# Revit family: Gira_004200
name_source: partatom
category: Electrical Fixtures
revit_build: Autodesk Revit 2017 (Build: 20160225_1515(x64)
units: mm (PartAtom-declared; Revit-internal decimal feet)

## family parameters
Cut with Voids When Loaded = No
Host = Face
Maintain Annotation Orientation = Yes
Part Type = Normal
Room Calculation Point = No
Round Connector Dimension = Use Diameter
Shared = No

## types (1)
- Antennensteckd. GEDU 15 Einsatz
    Anschlussdämpfung bei 2150 MHz = 1,5 B
    Anschlussdämpfung bei 860 MHz = 1,5 B
    Anzahl der Auslässe = 2
    Ausführung = Durchgangsdose
    Available = Yes
    Category = Antennensteckdose
    Data sheet (1) = https://katalog.gira.de
    Default Elevation = 1219 mm
    Durchgangsdämpfung bei 2150 MHz = 0,1 B
    Durchgangsdämpfung bei 860 MHz = 0,1 B
    Fernspeisetauglich = No
    Frequenz = 4000000 - 2400000000
    GTIN = 4010337042006
    HAN = 004200
    HeinzeBIM = https://bimportal.heinze.de
    Kabelmodemtauglich = Yes
    Keynote = Einsatz_1fach
    Manufacturer URL = https://www.gira.de
    Name = Antennensteckd. GEDU 15 Einsatz
    Region = DE
    URL = http://katalog.gira.de

## geometry (parser evidence)
native form markers: Blend x2, Sweep x3
no freeform markers — native parametric forms only
